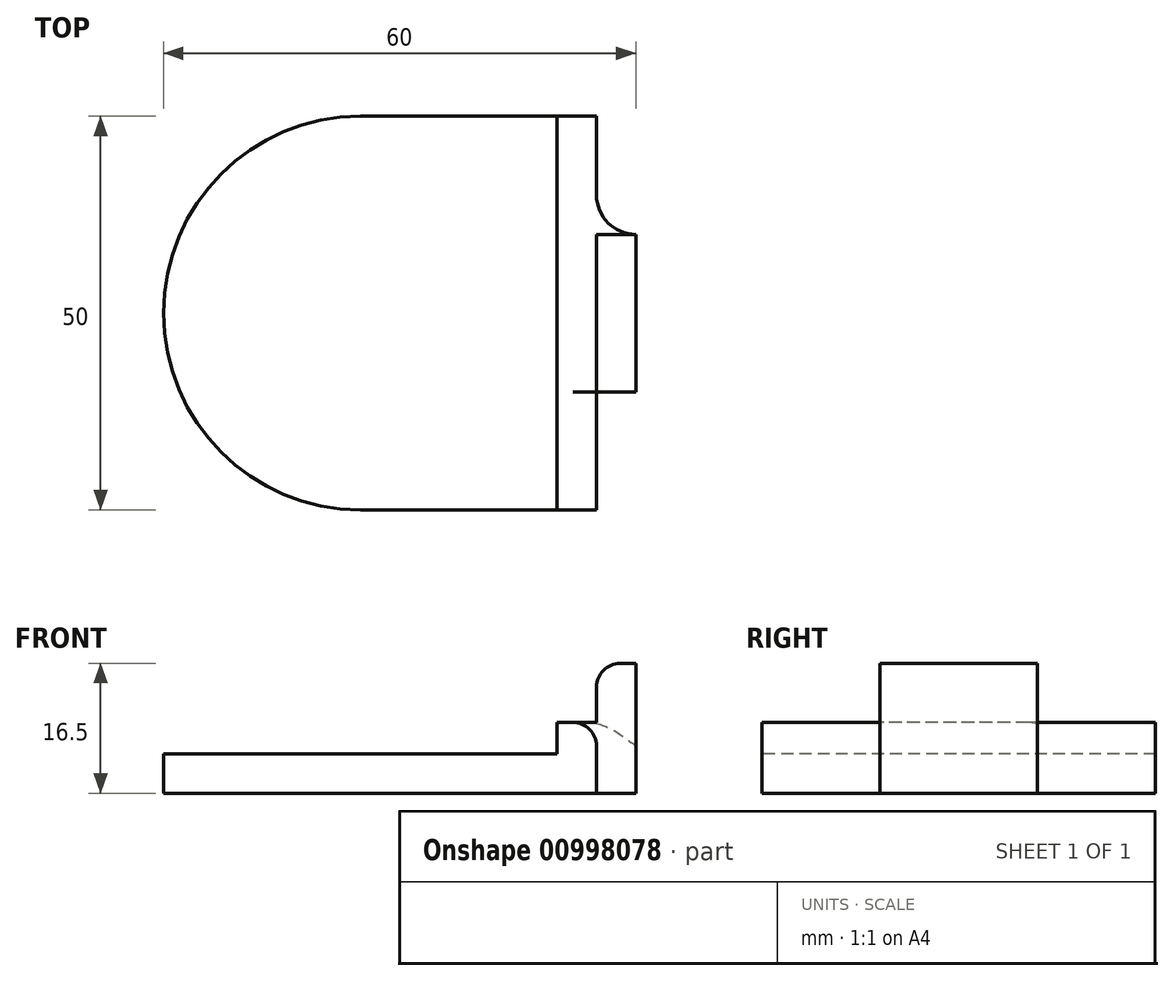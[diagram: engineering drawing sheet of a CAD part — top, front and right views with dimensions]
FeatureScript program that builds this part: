
annotation { "Feature Type Name" : "Feature", "Feature Type Description" : "" }
export const myFeature = defineFeature(function(context is Context, id is Id, definition is map)
    precondition{}
    {
        {
            var Q0;
            Q0=qCreatedBy(makeId("Top.planeOp"),FACE);
            var sketch = newSketch(context, id + "F0", { "sketchPlane" : qUnion([Q0])});
            skArc(sketch, "E0", {"start": v(0, 25) * mm, "mid": v(-25, 0) * mm, "end": v(0, -25) * mm});
            skLineSegment(sketch, "E1", {"start": v(0, 25) * mm, "end": v(30, 25) * mm});
            skLineSegment(sketch, "E2", {"start": v(30, 25) * mm, "end": v(30, 10) * mm});
            skLineSegment(sketch, "E3", {"start": v(30, -25) * mm, "end": v(0, -25) * mm});
            skLineSegment(sketch, "E4", {"start": v(35, 10) * mm, "end": v(35, -10) * mm});
            skLineSegment(sketch, "E5.trimOffspring", {"start": v(30, -10) * mm, "end": v(30, -25) * mm});
            skLineSegment(sketch, "E6", {"start": v(25, 36.59) * mm, "end": v(25, -50.52) * mm, "construction": true});
            skLineSegment(sketch, "E7", {"start": v(35, 10) * mm, "end": v(30, 10) * mm});
            skLineSegment(sketch, "E8", {"start": v(35, -10) * mm, "end": v(30, -10) * mm});
            skSolve(sketch);
        }
        {
            var Q0;
            Q0 = qSketchRegion(id + "F0", true);
            extrude(context, id + "F1", {"entities" : qUnion([Q0]), "depth" : 5 * mm, "offsetDistance" : 25 * mm});
        }
        {
            var Q0;
            Q0=makeQuery(id+"F1.opExtrude","CAP_FACE",FACE,{"disambiguationData":[OSD([sQuery(id+"F0.wireOp",EDGE,"E0"),sQuery(id+"F0.wireOp",EDGE,"E1"),sQuery(id+"F0.wireOp",EDGE,"E2"),sQuery(id+"F0.wireOp",EDGE,"E3"),sQuery(id+"F0.wireOp",EDGE,"PhaDR7OC-UvZV-PQvN-lx9v-YOrAoBFy80QW"),sQuery(id+"F0.wireOp",EDGE,"E4"),sQuery(id+"F0.wireOp",EDGE,"2lL8GISg-aMDv-ctMo-QciD-jeyDQ6myVX5a"),sQuery(id+"F0.wireOp",EDGE,"E5.trimOffspring"),sQuery(id+"F0.wireOp",EDGE,"222a972c-09bd-447b-b472-3dc0105ff7ce.filletArc"),sQuery(id+"F0.wireOp",EDGE,"fd7c0b0c-4f70-4964-b1c4-67f476bfda56.filletArc")])],"isStart":false});
            var sketch = newSketch(context, id + "F2", { "sketchPlane" : qUnion([Q0])});
            skLineSegment(sketch, "E9.bottom", {"start": v(30, 25) * mm, "end": v(25, 25) * mm});
            skLineSegment(sketch, "E9.top", {"start": v(30, -25) * mm, "end": v(25, -25) * mm});
            skLineSegment(sketch, "E9.left", {"start": v(30, 25) * mm, "end": v(30, -25) * mm});
            skLineSegment(sketch, "E9.right", {"start": v(25, 25) * mm, "end": v(25, -25) * mm});
            skSolve(sketch);
        }
        {
            var Q0;
            Q0 = qSketchRegion(id + "F2", true);
            extrude(context, id + "F3", {"entities" : qUnion([Q0]), "operationType" : NewBodyOperationType.ADD, "depth" : 4 * mm, "offsetDistance" : 25 * mm});
        }
        {
            var Q0;
            {var subQ0=sQuery(id+"F0.wireOp",EDGE,"2lL8GISg-aMDv-ctMo-QciD-jeyDQ6myVX5a");var subQ1=sQuery(id+"F0.wireOp",EDGE,"E4");var subQ2=sQuery(id+"F0.wireOp",EDGE,"PhaDR7OC-UvZV-PQvN-lx9v-YOrAoBFy80QW");var subQ3=sQuery(id+"F0.wireOp",EDGE,"E2");var subQ4=sQuery(id+"F0.wireOp",EDGE,"E5.trimOffspring");var subQ5=sQuery(id+"F0.wireOp",EDGE,"222a972c-09bd-447b-b472-3dc0105ff7ce.filletArc");var subQ6=sQuery(id+"F0.wireOp",EDGE,"fd7c0b0c-4f70-4964-b1c4-67f476bfda56.filletArc");Q0=makeQuery(id+"F3.boolean.opBoolean","SPLIT",FACE,{"disambiguationData":[TD([makeQuery(id+"F1.opExtrude","SWEPT_FACE",FACE,{"disambiguationData":[OSD([subQ3])]})])],"derivedFrom":makeQuery(id+"F1.opExtrude","CAP_FACE",FACE,{"disambiguationData":[OSD([sQuery(id+"F0.wireOp",EDGE,"E0"),sQuery(id+"F0.wireOp",EDGE,"E1"),subQ3,sQuery(id+"F0.wireOp",EDGE,"E3"),subQ2,subQ1,subQ0,subQ4,subQ5,subQ6])],"isStart":false})});}
            var sketch = newSketch(context, id + "F4", { "sketchPlane" : qUnion([Q0])});
            skLineSegment(sketch, "E10.bottom", {"start": v(35, 10) * mm, "end": v(30, 10) * mm});
            skLineSegment(sketch, "E10.top", {"start": v(35, -10) * mm, "end": v(30, -10) * mm});
            skLineSegment(sketch, "E10.left", {"start": v(35, 10) * mm, "end": v(35, -10) * mm});
            skLineSegment(sketch, "E10.right", {"start": v(30, 10) * mm, "end": v(30, -10) * mm});
            skSolve(sketch);
        }
        {
            var Q0;
            Q0 = qSketchRegion(id + "F4", true);
            extrude(context, id + "F5", {"entities" : qUnion([Q0]), "operationType" : NewBodyOperationType.ADD, "depth" : 11.5 * mm, "offsetDistance" : 25 * mm});
        }
        {
            var Q0;
            Q0=makeQuery(id+"F5.boolean.opBoolean","MERGE",EDGE,{"derivedFrom":[makeQuery(id+"F1.opExtrude","SWEPT_EDGE",EDGE,{"disambiguationData":[OSD([sQuery(id+"F0.wireOp",EDGE,"E5.trimOffspring"),sQuery(id+"F0.wireOp",EDGE,"E8")])]}),makeQuery(id+"F5.opExtrude","SWEPT_EDGE",EDGE,{"disambiguationData":[OSD([sQuery(id+"F4.wireOp",EDGE,"E10.top"),sQuery(id+"F4.wireOp",EDGE,"E10.right")])]})]});
            var Q1;
            Q1=makeQuery(id+"F1.opExtrude","SWEPT_EDGE",EDGE,{"disambiguationData":[OSD([sQuery(id+"F0.wireOp",EDGE,"E2"),sQuery(id+"F0.wireOp",EDGE,"E7")])]});
            fillet(context, id + "F6", {"entities" : qUnion([Q0, Q1]), "radius" : 5 * mm, "tangentPropagation" : true, "allowEdgeOverflow" : false});
        }
        {
            var Q0;
            {var subQ0=sQuery(id+"F2.wireOp",EDGE,"E9.left");Q0=makeQuery(id+"F5.boolean.opBoolean","SPLIT",EDGE,{"disambiguationData":[topologyDisambiguationEdgeConnected([makeQuery(id+"F3.opExtrude","CAP_FACE",FACE,{"disambiguationData":[OSD([sQuery(id+"F2.wireOp",EDGE,"E9.bottom"),sQuery(id+"F2.wireOp",EDGE,"E9.top"),subQ0,sQuery(id+"F2.wireOp",EDGE,"E9.right")])],"isStart":false}),makeQuery(id+"F5.opExtrude","SWEPT_FACE",FACE,{"disambiguationData":[OSD([sQuery(id+"F4.wireOp",EDGE,"E10.right")])]})])],"derivedFrom":makeQuery(id+"F3.opExtrude","CAP_EDGE",EDGE,{"disambiguationData":[OSD([subQ0])],"isStart":false})});}
            var Q1;
            {var subQ0=sQuery(id+"F2.wireOp",EDGE,"E9.left");Q1=makeQuery(id+"F6.opFillet","TWEAK_EDGE",EDGE,{"derivedFrom":[makeQuery(id+"F5.boolean.opBoolean","TWEAK_VERTEX",VERTEX,{"derivedFrom":[makeQuery(id+"F1.opExtrude","SWEPT_FACE",FACE,{"disambiguationData":[OSD([sQuery(id+"F0.wireOp",EDGE,"E7")])]}),makeQuery(id+"F3.opExtrude","CAP_FACE",FACE,{"disambiguationData":[OSD([sQuery(id+"F2.wireOp",EDGE,"E9.bottom"),sQuery(id+"F2.wireOp",EDGE,"E9.top"),subQ0,sQuery(id+"F2.wireOp",EDGE,"E9.right")])],"isStart":false}),makeQuery(id+"F3.boolean.opBoolean","MERGE",FACE,{"derivedFrom":[makeQuery(id+"F1.opExtrude","SWEPT_FACE",FACE,{"disambiguationData":[OSD([sQuery(id+"F0.wireOp",EDGE,"E2")])]}),makeQuery(id+"F1.opExtrude","SWEPT_FACE",FACE,{"disambiguationData":[OSD([sQuery(id+"F0.wireOp",EDGE,"E5.trimOffspring")])]}),makeQuery(id+"F3.opExtrude","SWEPT_FACE",FACE,{"disambiguationData":[OSD([subQ0])]})]}),makeQuery(id+"F5.opExtrude","SWEPT_FACE",FACE,{"disambiguationData":[OSD([sQuery(id+"F4.wireOp",EDGE,"E10.bottom")])]}),makeQuery(id+"F5.opExtrude","SWEPT_FACE",FACE,{"disambiguationData":[OSD([sQuery(id+"F4.wireOp",EDGE,"E10.right")])]})]})]});}
            var Q2;
            {var subQ0=sQuery(id+"F2.wireOp",EDGE,"E9.left");Q2=makeQuery(id+"F6.opFillet","TWEAK_EDGE",EDGE,{"derivedFrom":[makeQuery(id+"F5.boolean.opBoolean","TWEAK_VERTEX",VERTEX,{"derivedFrom":[makeQuery(id+"F1.opExtrude","SWEPT_FACE",FACE,{"disambiguationData":[OSD([sQuery(id+"F0.wireOp",EDGE,"E8")])]}),makeQuery(id+"F3.opExtrude","CAP_FACE",FACE,{"disambiguationData":[OSD([sQuery(id+"F2.wireOp",EDGE,"E9.bottom"),sQuery(id+"F2.wireOp",EDGE,"E9.top"),subQ0,sQuery(id+"F2.wireOp",EDGE,"E9.right")])],"isStart":false}),makeQuery(id+"F3.boolean.opBoolean","MERGE",FACE,{"derivedFrom":[makeQuery(id+"F1.opExtrude","SWEPT_FACE",FACE,{"disambiguationData":[OSD([sQuery(id+"F0.wireOp",EDGE,"E2")])]}),makeQuery(id+"F1.opExtrude","SWEPT_FACE",FACE,{"disambiguationData":[OSD([sQuery(id+"F0.wireOp",EDGE,"E5.trimOffspring")])]}),makeQuery(id+"F3.opExtrude","SWEPT_FACE",FACE,{"disambiguationData":[OSD([subQ0])]})]}),makeQuery(id+"F5.opExtrude","SWEPT_FACE",FACE,{"disambiguationData":[OSD([sQuery(id+"F4.wireOp",EDGE,"E10.top")])]}),makeQuery(id+"F5.opExtrude","SWEPT_FACE",FACE,{"disambiguationData":[OSD([sQuery(id+"F4.wireOp",EDGE,"E10.right")])]})]})]});}
            var Q3;
            Q3=makeQuery(id+"F5.opExtrude","CAP_EDGE",EDGE,{"disambiguationData":[OSD([sQuery(id+"F4.wireOp",EDGE,"E10.right")])],"isStart":false});
            fillet(context, id + "F7", {"entities" : qUnion([Q0, Q1, Q2, Q3]), "radius" : 3 * mm, "tangentPropagation" : true, "allowEdgeOverflow" : false});
        }
    });
